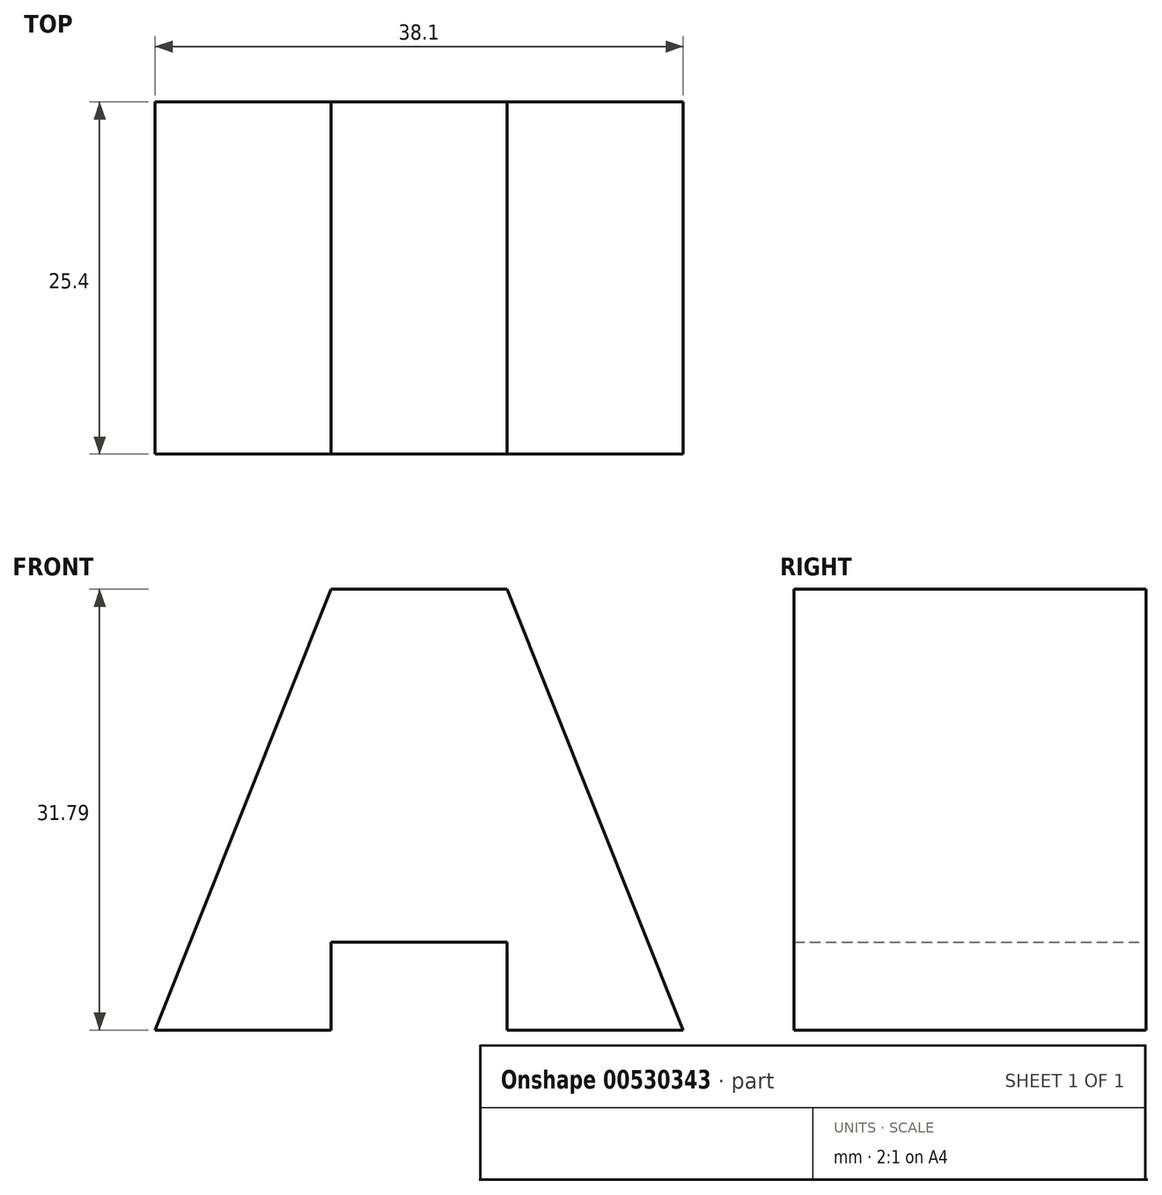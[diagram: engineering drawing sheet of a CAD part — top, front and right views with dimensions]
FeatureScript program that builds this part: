
annotation { "Feature Type Name" : "Feature", "Feature Type Description" : "" }
export const myFeature = defineFeature(function(context is Context, id is Id, definition is map)
    precondition{}
    {
        {
            var Q0;
            Q0=qCreatedBy(makeId("Front.planeOp"),FACE);
            var sketch = newSketch(context, id + "F0", { "sketchPlane" : qUnion([Q0])});
            skLineSegment(sketch, "E0", {"start": v(-67.2, -0.04) * mm, "end": v(-54.5, -0.04) * mm});
            skLineSegment(sketch, "E1", {"start": v(-54.5, -0.04) * mm, "end": v(-54.5, 6.3) * mm});
            skLineSegment(sketch, "E2", {"start": v(-54.5, 6.3) * mm, "end": v(-41.8, 6.3) * mm});
            skLineSegment(sketch, "E3", {"start": v(-41.8, 6.3) * mm, "end": v(-41.8, -0.04) * mm});
            skLineSegment(sketch, "E4", {"start": v(-41.8, -0.04) * mm, "end": v(-29.1, -0.04) * mm});
            skLineSegment(sketch, "E5", {"start": v(-67.2, -0.04) * mm, "end": v(-54.5, 31.75) * mm});
            skLineSegment(sketch, "E6", {"start": v(-54.5, 31.75) * mm, "end": v(-41.8, 31.75) * mm});
            skLineSegment(sketch, "E7", {"start": v(-41.8, 31.75) * mm, "end": v(-29.1, -0.04) * mm});
            skPoint(sketch, "E8.startSnap0", {"position": v(-48.15, 31.75) * mm});
            skSolve(sketch);
        }
        {
            var Q0;
            Q0 = qSketchRegion(id + "F0", true);
            extrude(context, id + "F1", {"entities" : qUnion([Q0]), "depth" : 25.4 * mm, "offsetDistance" : 25.4 * mm});
        }
    });
